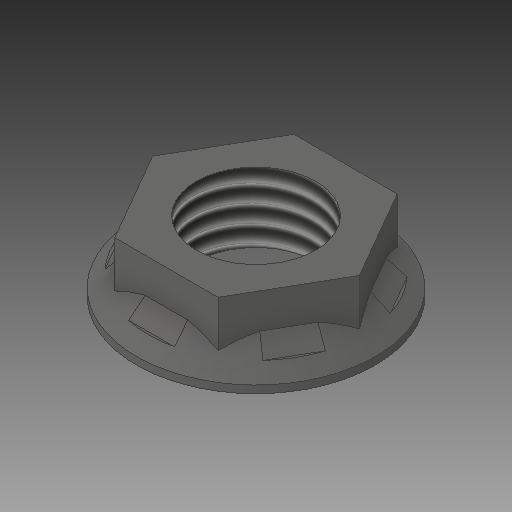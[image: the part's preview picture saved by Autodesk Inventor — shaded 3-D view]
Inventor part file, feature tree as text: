
AUTODESK INVENTOR PART (.ipt)
format: ipt  version: 2019 (Build 230136000, 136)  size: 161,792 bytes
history: native  units: mm
features: other x3, sketch x3
ambient origin geometry x8: Origin, YZ Plane, XZ Plane, XY Plane, X Axis, Y Axis, Z Axis, Center Point
bodies: Solid1 (feature_tree)
feature tree (6):
  other  "Nylon Nut.ipt"
  other  "Solid1::Nylon Nut.ipt"
  other  "TaggingFeature1"
  sketch  "Sketch2"  dims[d0=10.0mm]
  sketch  "Sketch3"
  sketch  "Sketch4"
